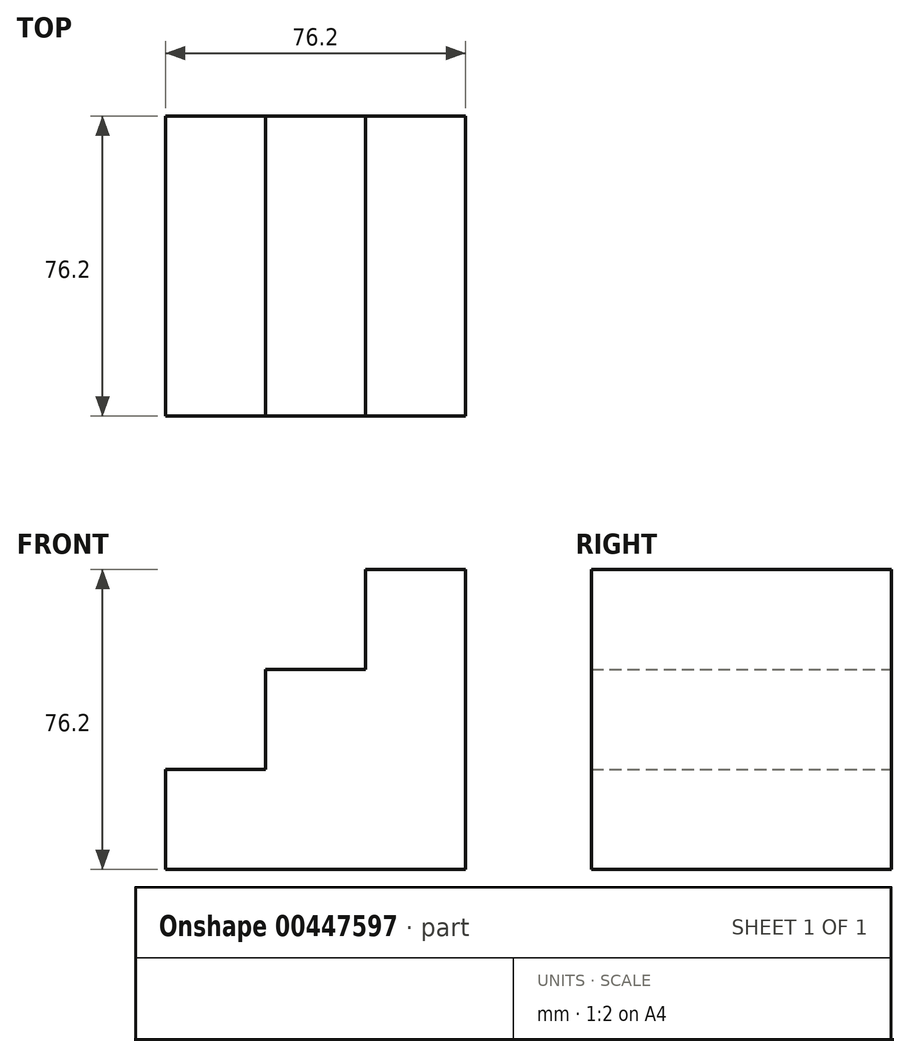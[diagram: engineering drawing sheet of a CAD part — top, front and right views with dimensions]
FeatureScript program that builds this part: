
annotation { "Feature Type Name" : "Feature", "Feature Type Description" : "" }
export const myFeature = defineFeature(function(context is Context, id is Id, definition is map)
    precondition{}
    {
        {
            var Q0;
            Q0=qCreatedBy(makeId("Front.planeOp"),FACE);
            var sketch = newSketch(context, id + "F0", { "sketchPlane" : qUnion([Q0])});
            skLineSegment(sketch, "E0", {"start": v(-46.05, 0) * mm, "end": v(30.15, 0) * mm});
            skLineSegment(sketch, "E1", {"start": v(30.15, 0) * mm, "end": v(30.15, 76.2) * mm});
            skLineSegment(sketch, "E2", {"start": v(30.15, 76.2) * mm, "end": v(4.75, 76.2) * mm});
            skLineSegment(sketch, "E3", {"start": v(4.75, 76.2) * mm, "end": v(4.75, 50.8) * mm});
            skLineSegment(sketch, "E4", {"start": v(4.75, 50.8) * mm, "end": v(-20.65, 50.8) * mm});
            skLineSegment(sketch, "E5", {"start": v(-20.65, 50.8) * mm, "end": v(-20.65, 25.4) * mm});
            skLineSegment(sketch, "E6", {"start": v(-20.65, 25.4) * mm, "end": v(-46.05, 25.4) * mm});
            skLineSegment(sketch, "E7", {"start": v(-46.05, 25.4) * mm, "end": v(-46.05, 0) * mm});
            skSolve(sketch);
        }
        {
            var Q0;
            Q0 = qSketchRegion(id + "F0", true);
            extrude(context, id + "F1", {"entities" : qUnion([Q0]), "depth" : 76.2 * mm});
        }
    });
